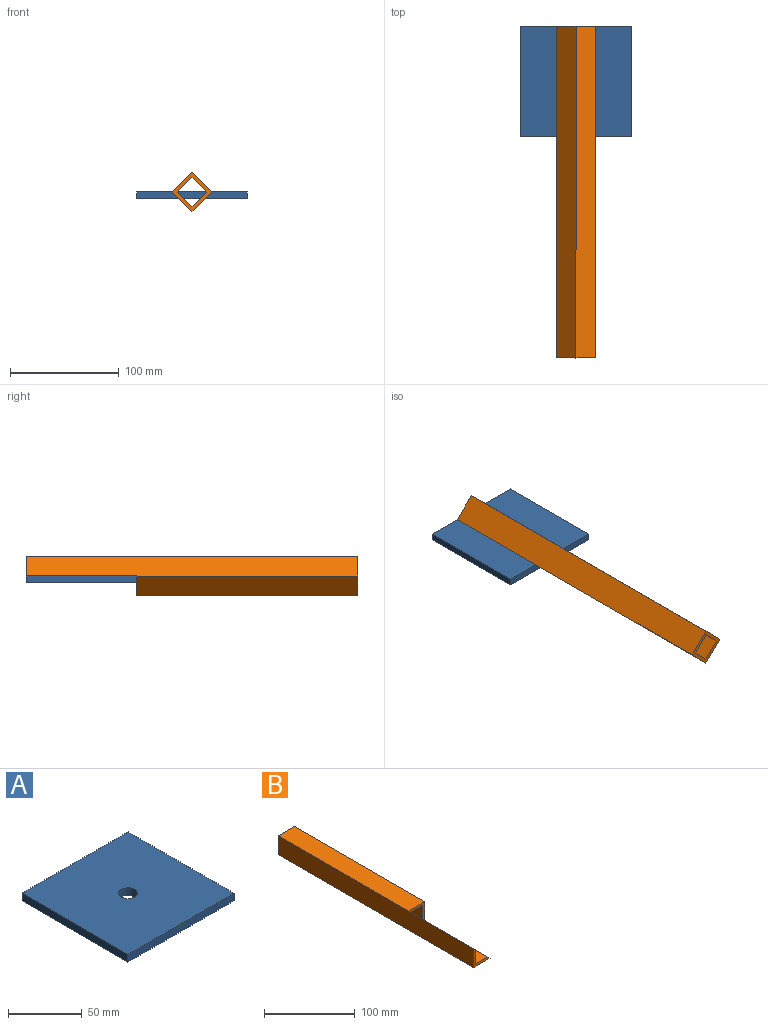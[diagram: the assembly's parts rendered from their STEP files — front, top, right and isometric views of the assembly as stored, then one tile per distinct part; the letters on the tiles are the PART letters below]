
ASSEMBLY  parts=2 mates=1
PART A: 7 faces, bbox 101.6x101.6x6.4 mm
  f0: plane 101.6x6.35mm, normal (0,-1,0), area 645.2mm2, adj f1,f4,f5,f6
  f1: plane 101.6x6.35mm, normal (1,0,0), area 645.2mm2, adj f0,f2,f5,f6
  f2: plane 101.6x6.35mm, normal (0,1,0), area 645.2mm2, adj f1,f4,f5,f6
  f3: cylinder r=6.35mm len=12.7mm, axis (0,0,-1), area 253.4mm2, adj f5,f6
  f4: plane 101.6x6.35mm, normal (-1,0,0), area 645.2mm2, adj f0,f2,f5,f6
  f5: plane 101.6x101.6mm, normal (0,0,1), area 10195.9mm2, adj f0,f1,f2,f3,f4
  f6: plane 101.6x101.6mm, normal (0,0,-1), area 10195.9mm2, adj f0,f1,f2,f3,f4
PART B: 13 faces, bbox 25.4x304.8x25.4 mm
  f0: plane 203.2x25.4mm, normal (1,0,0), area 5161.3mm2, adj f1,f4,f9,f10
  f1: plane 203.2x25.4mm, normal (0,0,1), area 5161.3mm2, adj f0,f7,f9,f10
  f2: plane 203.2x19.05mm, normal (0,0,-1), area 3871mm2, adj f3,f5,f9,f10
  f3: plane 203.2x19.05mm, normal (-1,0,0), area 3871mm2, adj f2,f6,f9,f10
  f4: plane 304.8x25.4mm, normal (0,0,-1), area 7741.9mm2, adj f0,f7,f8,f9,f11
  f5: plane 304.8x19.05mm, normal (1,0,0), area 5806.4mm2, adj f2,f6,f8,f9,f12
  f6: plane 304.8x19.05mm, normal (0,0,1), area 5806.4mm2, adj f3,f5,f8,f9,f11
  f7: plane 304.8x25.4mm, normal (-1,0,0), area 7741.9mm2, adj f1,f4,f8,f9,f12
  f8: plane 25.4x25.4mm, normal (0,-1,0), area 141.1mm2, adj f4,f5,f6,f7,f11,f12
  f9: plane 25.4x25.4mm, normal (0,1,0), area 282.3mm2, adj f0,f1,f2,f3,f4,f5,f6,f7
  f10: plane 25.4x25.4mm, normal (0,-1,0), area 141.1mm2, adj f0,f1,f2,f3,f11,f12
  f11: plane 101.6x3.18mm, normal (0.71,0,0.71), area 456.2mm2, adj f4,f6,f8,f10
  f12: plane 101.6x3.18mm, normal (0.71,0,0.71), area 456.2mm2, adj f5,f7,f8,f10
PLACE A t=(-18.07,-9.69,24.34)mm fixed
PLACE B rot(axis=(0.92,0,-0.38),180deg) t=(-18.07,-263.69,30.69)mm
MATE fastened A.f0 <-> B.f10  axis (0,-1,0) through (-18.07,-60.49,30.69)mm
